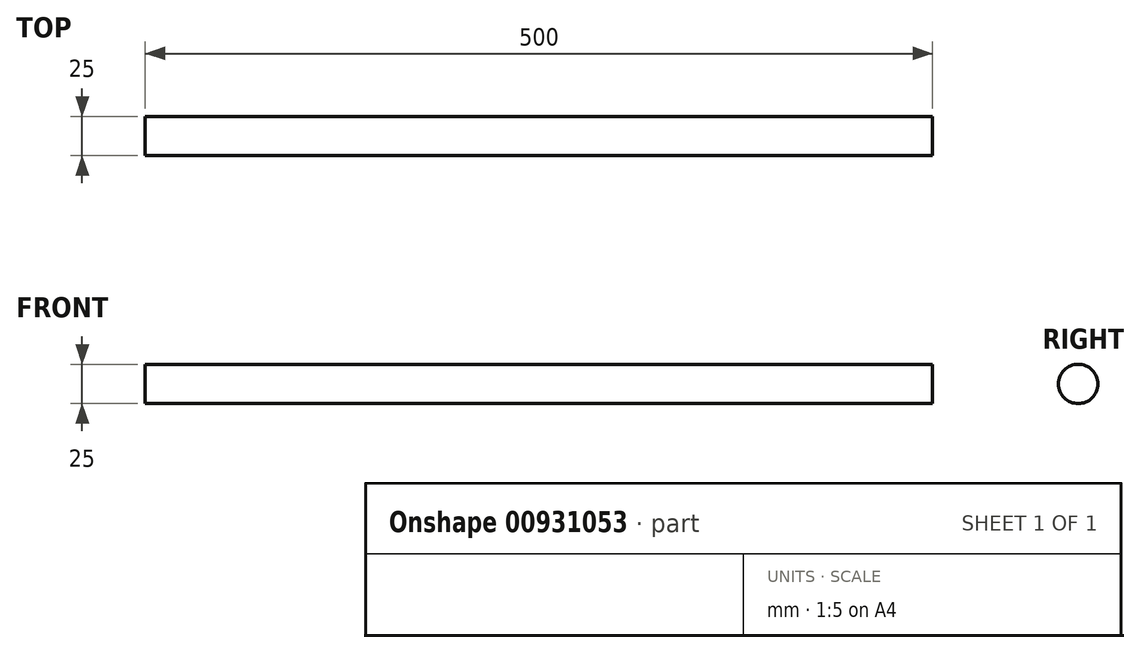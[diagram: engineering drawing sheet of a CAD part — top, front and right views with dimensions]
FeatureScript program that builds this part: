
annotation { "Feature Type Name" : "Feature", "Feature Type Description" : "" }
export const myFeature = defineFeature(function(context is Context, id is Id, definition is map)
    precondition{}
    {
        {
            var Q0;
            Q0=qCreatedBy(makeId("Right.planeOp"),FACE);
            var sketch = newSketch(context, id + "F0", { "sketchPlane" : qUnion([Q0])});
            skCircle(sketch, "E0", {"center": v(0, 0) * mm, "radius": 12.5 * mm});
            skSolve(sketch);
        }
        {
            var Q0;
            Q0=makeQuery(id+"F0.imprint","IMPRINT",FACE,{"disambiguationData":[TD([[makeQuery(id+"F0.imprint","IMPRINT",EDGE,{"derivedFrom":sQuery(id+"F0.wireOp",EDGE,"E0")}),1.0]])]});
            extrude(context, id + "F1", {"entities" : qUnion([Q0]), "depth" : 500 * mm, "offsetDistance" : 25 * mm, "symmetric" : true});
        }
    });
